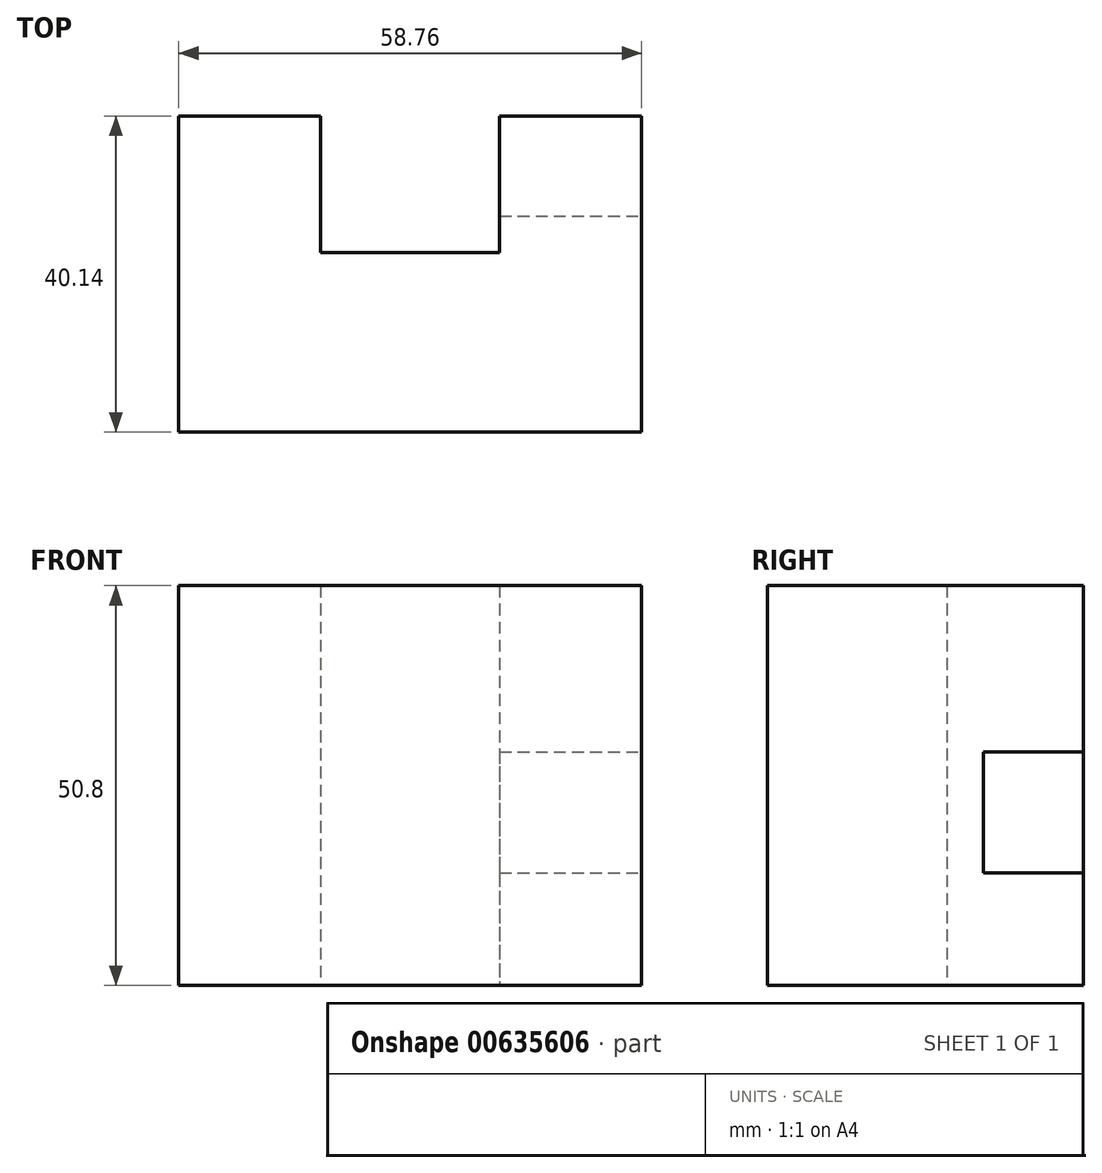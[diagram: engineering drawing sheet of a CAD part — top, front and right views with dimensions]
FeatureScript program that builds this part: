
annotation { "Feature Type Name" : "Feature", "Feature Type Description" : "" }
export const myFeature = defineFeature(function(context is Context, id is Id, definition is map)
    precondition{}
    {
        {
            var Q0;
            Q0=qCreatedBy(makeId("Top.planeOp"),FACE);
            var sketch = newSketch(context, id + "F0", { "sketchPlane" : qUnion([Q0])});
            skLineSegment(sketch, "E0.bottom", {"start": v(0, 0) * mm, "end": v(58.76, 0) * mm});
            skLineSegment(sketch, "E0.top", {"start": v(0, 40.14) * mm, "end": v(18.02, 40.14) * mm});
            skLineSegment(sketch, "E0.left", {"start": v(0, 0) * mm, "end": v(0, 40.14) * mm});
            skLineSegment(sketch, "E0.right", {"start": v(58.76, 0) * mm, "end": v(58.76, 40.14) * mm});
            skLineSegment(sketch, "E1.top", {"start": v(18.02, 22.82) * mm, "end": v(40.74, 22.82) * mm});
            skLineSegment(sketch, "E1.left", {"start": v(18.02, 40.14) * mm, "end": v(18.02, 22.82) * mm});
            skLineSegment(sketch, "E1.right", {"start": v(40.74, 40.14) * mm, "end": v(40.74, 22.82) * mm});
            skLineSegment(sketch, "E2.trimOffspring", {"start": v(40.74, 40.14) * mm, "end": v(58.76, 40.14) * mm});
            skSolve(sketch);
        }
        {
            var Q0;
            Q0 = qSketchRegion(id + "F0", true);
            extrude(context, id + "F1", {"entities" : qUnion([Q0]), "depth" : 50.8 * mm, "offsetDistance" : 25.4 * mm});
        }
        {
            var Q0;
            Q0=makeQuery(id+"F1.opExtrude","SWEPT_FACE",FACE,{"disambiguationData":[OSD([sQuery(id+"F0.wireOp",EDGE,"E2.trimOffspring")])]});
            var sketch = newSketch(context, id + "F2", { "sketchPlane" : qUnion([Q0])});
            skLineSegment(sketch, "E3.bottom", {"start": v(-40.74, 14.33) * mm, "end": v(-58.76, 14.33) * mm});
            skLineSegment(sketch, "E3.top", {"start": v(-40.74, 29.66) * mm, "end": v(-58.76, 29.66) * mm});
            skLineSegment(sketch, "E3.left", {"start": v(-40.74, 14.33) * mm, "end": v(-40.74, 29.66) * mm});
            skLineSegment(sketch, "E3.right", {"start": v(-58.76, 14.33) * mm, "end": v(-58.76, 29.66) * mm});
            skSolve(sketch);
        }
        {
            var Q0;
            Q0 = qSketchRegion(id + "F2", true);
            extrude(context, id + "F3", {"entities" : qUnion([Q0]), "operationType" : NewBodyOperationType.REMOVE, "oppositeDirection" : true, "depth" : 12.7 * mm, "offsetDistance" : 25.4 * mm});
        }
    });
